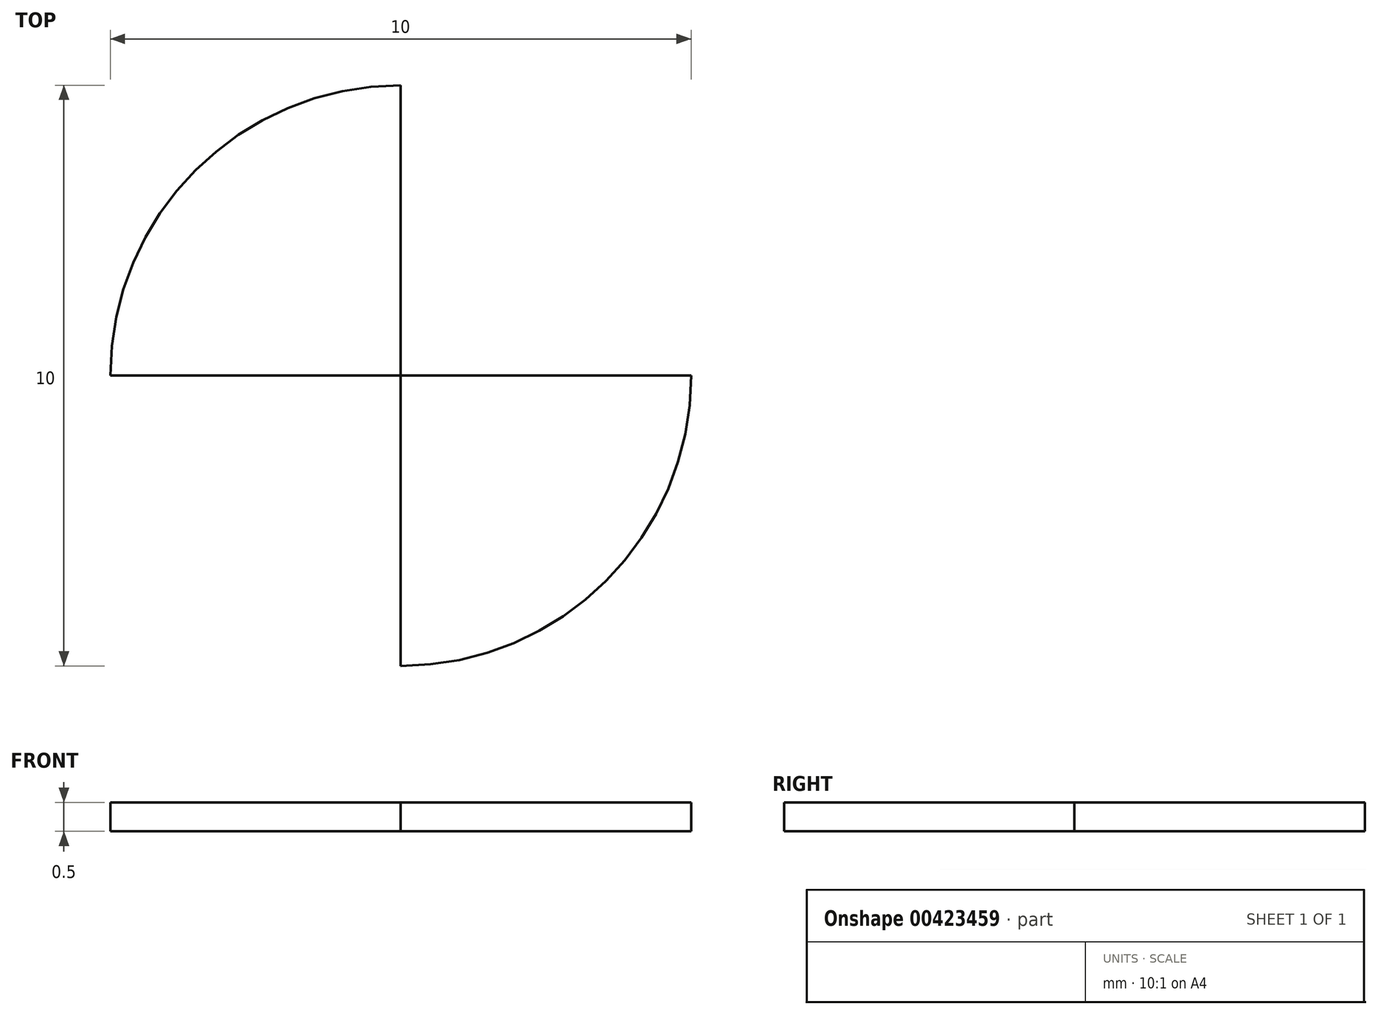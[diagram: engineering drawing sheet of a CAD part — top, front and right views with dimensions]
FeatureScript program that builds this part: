
annotation { "Feature Type Name" : "Feature", "Feature Type Description" : "" }
export const myFeature = defineFeature(function(context is Context, id is Id, definition is map)
    precondition{}
    {
        {
            var Q0;
            Q0=qCreatedBy(makeId("Top.planeOp"),FACE);
            var sketch = newSketch(context, id + "F0", { "sketchPlane" : qUnion([Q0])});
            skCircle(sketch, "E0", {"center": v(0, 0) * mm, "radius": 5 * mm});
            skLineSegment(sketch, "E1", {"start": v(-5, 0) * mm, "end": v(5, 0) * mm});
            skLineSegment(sketch, "E2", {"start": v(0, 5) * mm, "end": v(0, -5) * mm});
            skSolve(sketch);
        }
        {
            var Q0;
            {var subQ0=sQuery(id+"F0.wireOp",EDGE,"E2");var subQ1=sQuery(id+"F0.wireOp",EDGE,"E0");var subQ2=makeQuery(id+"F0.imprint","INTERSECT",VERTEX,{"disambiguationData":[OD(0.0)],"derivedFrom":[subQ1,subQ0]});Q0=makeQuery(id+"F0.imprint","IMPRINT",FACE,{"disambiguationData":[TD([[makeQuery(id+"F0.imprint","IMPRINT",EDGE,{"disambiguationData":[TD([[subQ2,-1.0]])],"derivedFrom":subQ1}),1.0]])]});}
            var Q1;
            {var subQ0=sQuery(id+"F0.wireOp",EDGE,"E1");var subQ1=sQuery(id+"F0.wireOp",EDGE,"E0");var subQ2=makeQuery(id+"F0.imprint","INTERSECT",VERTEX,{"disambiguationData":[OD(0.0)],"derivedFrom":[subQ1,subQ0]});Q1=makeQuery(id+"F0.imprint","IMPRINT",FACE,{"disambiguationData":[TD([[makeQuery(id+"F0.imprint","IMPRINT",EDGE,{"disambiguationData":[TD([[subQ2,1.0]])],"derivedFrom":subQ1}),1.0]])]});}
            extrude(context, id + "F1", {"entities" : qUnion([Q0, Q1]), "depth" : 0.5 * mm, "offsetDistance" : 25 * mm});
        }
    });
